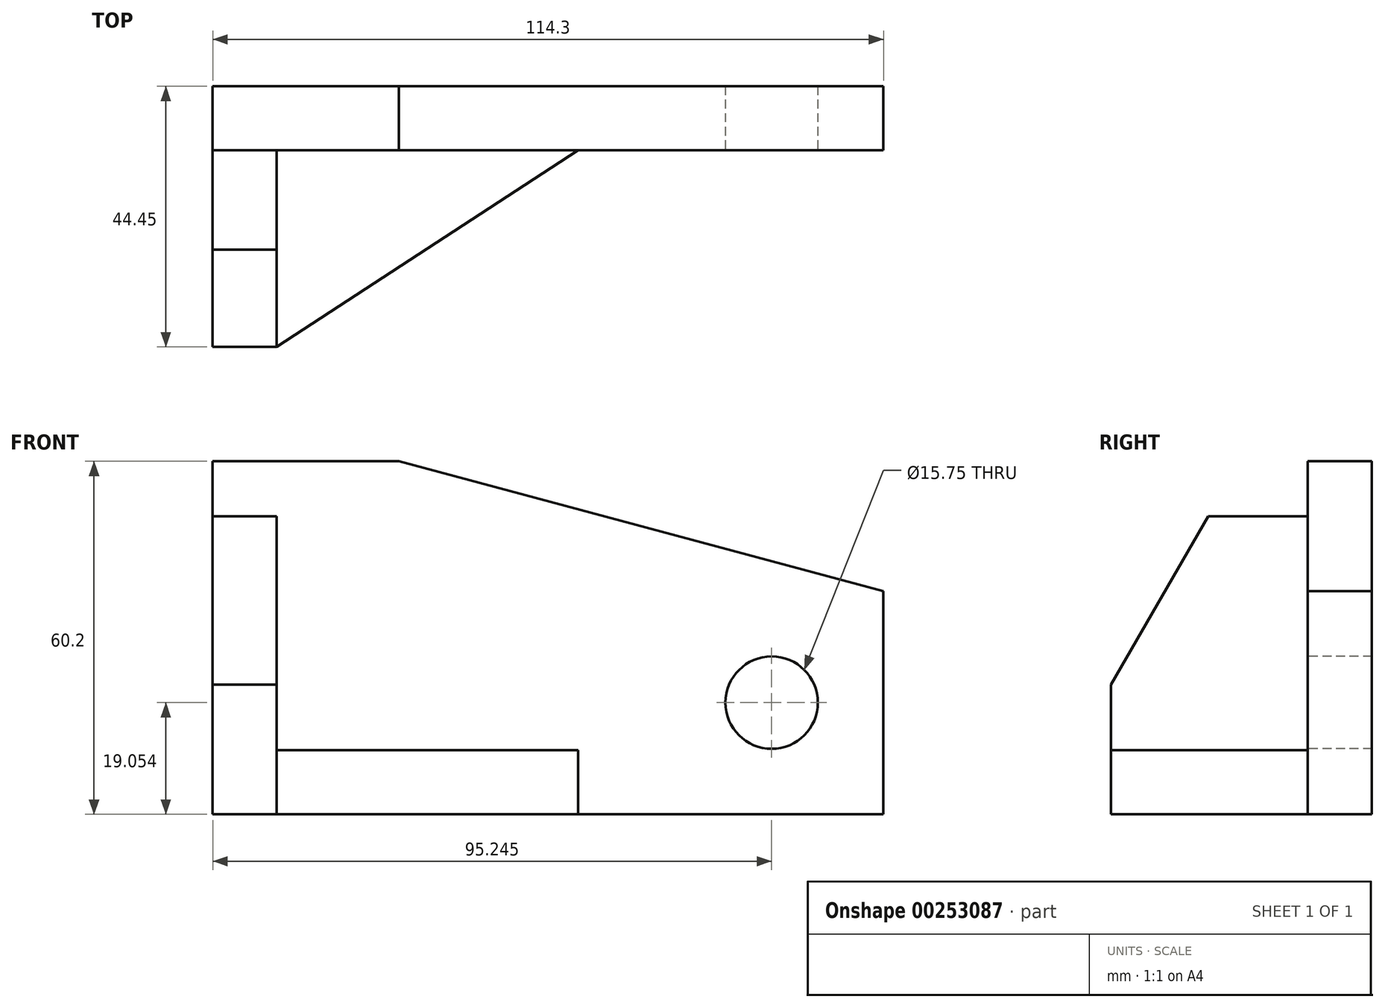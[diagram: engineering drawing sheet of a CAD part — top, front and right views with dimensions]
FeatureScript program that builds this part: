
annotation { "Feature Type Name" : "Feature", "Feature Type Description" : "" }
export const myFeature = defineFeature(function(context is Context, id is Id, definition is map)
    precondition{}
    {
        {
            var Q0;
            Q0=qCreatedBy(makeId("Front.planeOp"),FACE);
            var sketch = newSketch(context, id + "F0", { "sketchPlane" : qUnion([Q0])});
            skLineSegment(sketch, "E0", {"start": v(-62.24, 46.23) * mm, "end": v(-30.5, 46.23) * mm});
            skLineSegment(sketch, "E1", {"start": v(-62.24, 46.23) * mm, "end": v(-62.24, -13.97) * mm});
            skLineSegment(sketch, "E2", {"start": v(-62.24, -13.97) * mm, "end": v(52.06, -13.97) * mm});
            skLineSegment(sketch, "E3", {"start": v(-30.5, 46.23) * mm, "end": v(52.06, 24.11) * mm});
            skLineSegment(sketch, "E4", {"start": v(52.06, 24.11) * mm, "end": v(52.06, -13.97) * mm});
            skCircle(sketch, "E5", {"center": v(33, 5.08) * mm, "radius": 7.87 * mm});
            skLineSegment(sketch, "E6", {"start": v(-62.24, 36.83) * mm, "end": v(-51.32, 36.83) * mm});
            skLineSegment(sketch, "E7", {"start": v(-51.32, 36.83) * mm, "end": v(-51.32, -13.97) * mm});
            skLineSegment(sketch, "E8", {"start": v(-51.32, -3.04) * mm, "end": v(1.26, -3.04) * mm});
            skLineSegment(sketch, "E9", {"start": v(1.26, -3.04) * mm, "end": v(1.26, -13.97) * mm});
            skPoint(sketch, "E10.end.orphan", {"position": v(-51.32, 8.13) * mm});
            skSolve(sketch);
        }
        {
            var Q0;
            {var subQ4=sQuery(id+"F0.wireOp",EDGE,"E8");Q0=makeQuery(id+"F0.imprint","IMPRINT",FACE,{"disambiguationData":[TD([[makeQuery(id+"F0.imprint","IMPRINT",EDGE,{"derivedFrom":subQ4}),-1.0]])]});}
            var Q1;
            {var subQ4=sQuery(id+"F0.wireOp",EDGE,"E10");Q1=makeQuery(id+"F0.imprint","IMPRINT",FACE,{"disambiguationData":[TD([[makeQuery(id+"F0.imprint","IMPRINT",EDGE,{"derivedFrom":subQ4}),-1.0]])]});}
            var Q2;
            {var subQ6=sQuery(id+"F0.wireOp",EDGE,"E0");Q2=makeQuery(id+"F0.imprint","IMPRINT",FACE,{"disambiguationData":[TD([[makeQuery(id+"F0.imprint","IMPRINT",EDGE,{"derivedFrom":subQ6}),-1.0]])]});}
            var Q3;
            {var subQ6=sQuery(id+"F0.wireOp",EDGE,"E0");Q3=makeQuery(id+"F0.imprint","IMPRINT",FACE,{"disambiguationData":[TD([[makeQuery(id+"F0.imprint","IMPRINT",EDGE,{"derivedFrom":subQ6}),-1.0]])]});}
            var Q4;
            {var subQ1=sQuery(id+"F0.wireOp",EDGE,"E6");Q4=makeQuery(id+"F0.imprint","IMPRINT",FACE,{"disambiguationData":[TD([[makeQuery(id+"F0.imprint","IMPRINT",EDGE,{"derivedFrom":subQ1}),-1.0]])]});}
            extrude(context, id + "F1", {"entities" : qUnion([Q0, Q1, Q2, Q3, Q4]), "oppositeDirection" : true, "depth" : 10.92 * mm});
        }
        {
            var Q0;
            {var subQ1=sQuery(id+"F0.wireOp",EDGE,"E6");Q0=makeQuery(id+"F0.imprint","IMPRINT",FACE,{"disambiguationData":[TD([[makeQuery(id+"F0.imprint","IMPRINT",EDGE,{"derivedFrom":subQ1}),-1.0]])]});}
            var Q1;
            {var subQ4=sQuery(id+"F0.wireOp",EDGE,"E8");Q1=makeQuery(id+"F0.imprint","IMPRINT",FACE,{"disambiguationData":[TD([[makeQuery(id+"F0.imprint","IMPRINT",EDGE,{"derivedFrom":subQ4}),-1.0]])]});}
            extrude(context, id + "F2", {"entities" : qUnion([Q0, Q1]), "operationType" : NewBodyOperationType.ADD, "depth" : 33.53 * mm});
        }
        {
            var Q0;
            Q0=makeQuery(id+"F2.opExtrude","CAP_EDGE",EDGE,{"disambiguationData":[OSD([sQuery(id+"F0.wireOp",EDGE,"E6")])],"isStart":false});
            chamfer(context, id + "F3", {"entities" : qUnion([Q0]), "chamferType" : ChamferType.OFFSET_ANGLE, "width" : 28.7 * mm, "oppositeDirection" : true, "angle" : 30 * degree, "tangentPropagation" : true});
        }
        {
            var Q0;
            Q0=makeQuery(id+"F2.opExtrude","SWEPT_FACE",FACE,{"disambiguationData":[OSD([sQuery(id+"F0.wireOp",EDGE,"E8")])]});
            var sketch = newSketch(context, id + "F4", { "sketchPlane" : qUnion([Q0])});
            skLineSegment(sketch, "E11", {"start": v(-51.32, 0) * mm, "end": v(1.26, 0) * mm});
            skLineSegment(sketch, "E12", {"start": v(1.26, 0) * mm, "end": v(1.26, -33.53) * mm});
            skLineSegment(sketch, "E13", {"start": v(1.26, -33.53) * mm, "end": v(-51.32, -33.53) * mm});
            skLineSegment(sketch, "E14", {"start": v(-51.32, -33.53) * mm, "end": v(0, 0) * mm});
            skSolve(sketch);
        }
        {
            var Q0;
            {var subQ0=sQuery(id+"F4.wireOp",EDGE,"E12");Q0=makeQuery(id+"F4.imprint","IMPRINT",FACE,{"disambiguationData":[TD([[makeQuery(id+"F4.imprint","IMPRINT",EDGE,{"derivedFrom":subQ0}),1.0]])]});}
            extrude(context, id + "F5", {"entities" : qUnion([Q0]), "operationType" : NewBodyOperationType.REMOVE, "oppositeDirection" : true, "depth" : 25.4 * mm});
        }
    });
